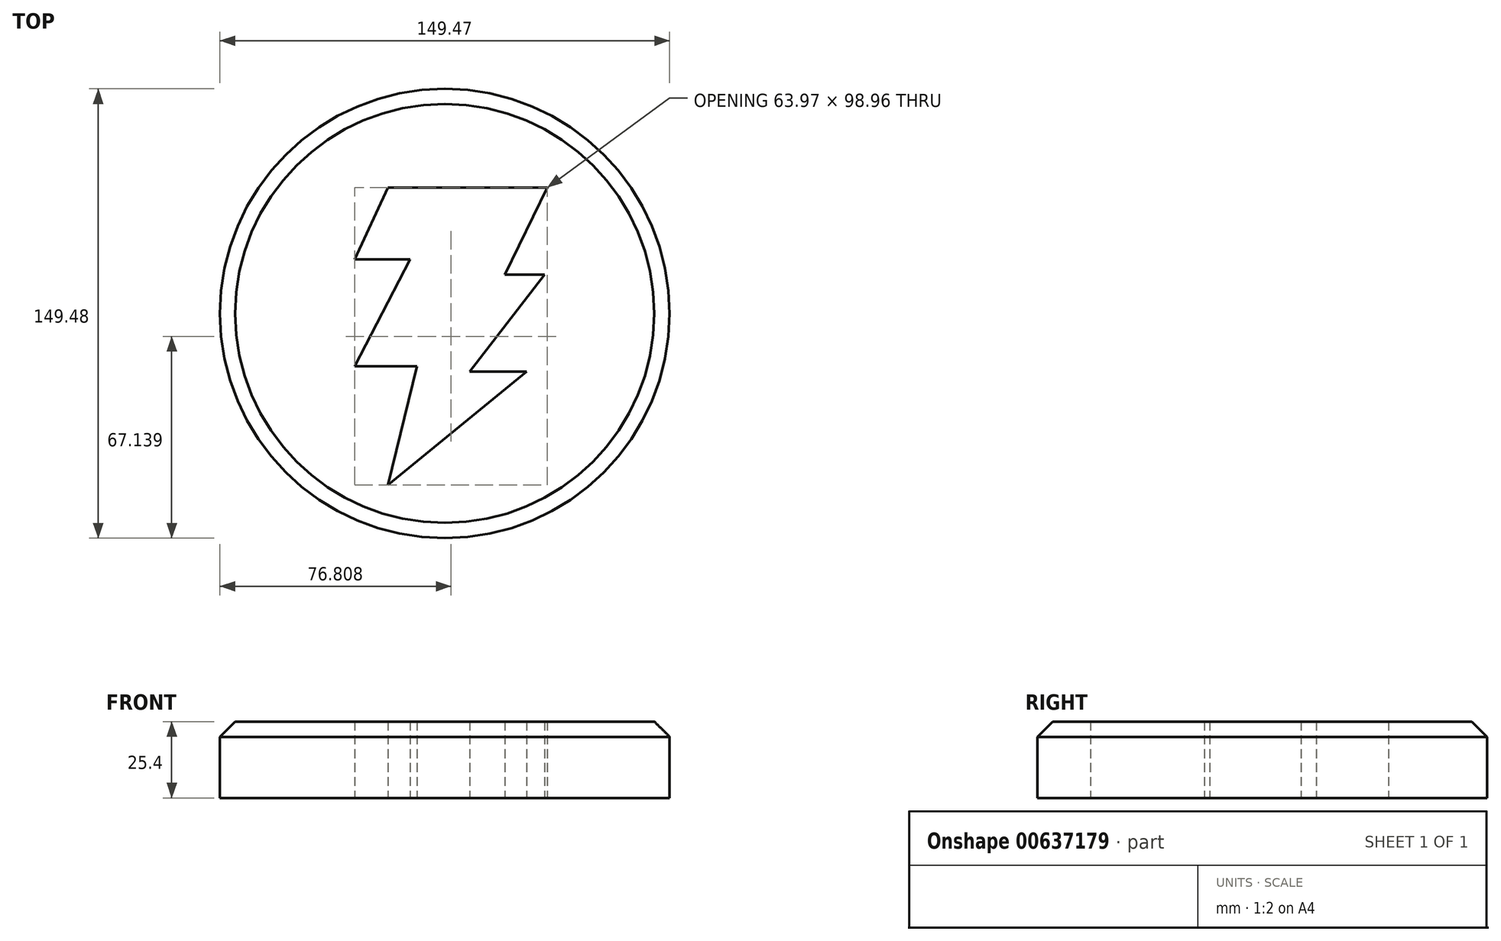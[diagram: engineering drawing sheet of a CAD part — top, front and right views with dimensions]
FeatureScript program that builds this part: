
annotation { "Feature Type Name" : "Feature", "Feature Type Description" : "" }
export const myFeature = defineFeature(function(context is Context, id is Id, definition is map)
    precondition{}
    {
        {
            var Q0;
            Q0=qCreatedBy(makeId("Top.planeOp"),FACE);
            var sketch = newSketch(context, id + "F0", { "sketchPlane" : qUnion([Q0])});
            skLineSegment(sketch, "E0", {"start": v(-38.9, 41.88) * mm, "end": v(14.03, 41.88) * mm});
            skLineSegment(sketch, "E1", {"start": v(14.03, 41.88) * mm, "end": v(0, 12.88) * mm});
            skLineSegment(sketch, "E2", {"start": v(0, 12.88) * mm, "end": v(13.11, 12.88) * mm});
            skLineSegment(sketch, "E3", {"start": v(13.11, 12.88) * mm, "end": v(-11.74, -19.34) * mm});
            skLineSegment(sketch, "E4", {"start": v(-11.74, -19.34) * mm, "end": v(7.13, -19.34) * mm});
            skLineSegment(sketch, "E5", {"start": v(7.13, -19.34) * mm, "end": v(-38.9, -57.08) * mm});
            skLineSegment(sketch, "E6", {"start": v(-38.9, 41.88) * mm, "end": v(-49.94, 17.94) * mm});
            skLineSegment(sketch, "E7", {"start": v(-49.94, 17.94) * mm, "end": v(-31.53, 17.94) * mm});
            skLineSegment(sketch, "E8", {"start": v(-31.53, 17.94) * mm, "end": v(-49.94, -17.5) * mm});
            skLineSegment(sketch, "E9", {"start": v(-49.94, -17.5) * mm, "end": v(-29.23, -17.5) * mm});
            skLineSegment(sketch, "E10", {"start": v(-29.23, -17.5) * mm, "end": v(-38.9, -57.08) * mm});
            skCircle(sketch, "E11", {"center": v(-20.02, 0) * mm, "radius": 74.74 * mm});
            skSolve(sketch);
        }
        {
            var Q0;
            Q0=makeQuery(id+"F0.imprint","IMPRINT",FACE,{"disambiguationData":[TD([[makeQuery(id+"F0.imprint","IMPRINT",EDGE,{"derivedFrom":sQuery(id+"F0.wireOp",EDGE,"E0")}),1.0]])]});
            extrude(context, id + "F1", {"entities" : qUnion([Q0]), "depth" : 25.4 * mm, "offsetDistance" : 25.4 * mm});
        }
        {
            var Q0;
            Q0=makeQuery(id+"F1.opExtrude","CAP_EDGE",EDGE,{"disambiguationData":[OSD([sQuery(id+"F0.wireOp",EDGE,"E11")])],"isStart":false});
            chamfer(context, id + "F2", {"entities" : qUnion([Q0]), "width" : 5.08 * mm, "tangentPropagation" : true});
        }
    });
